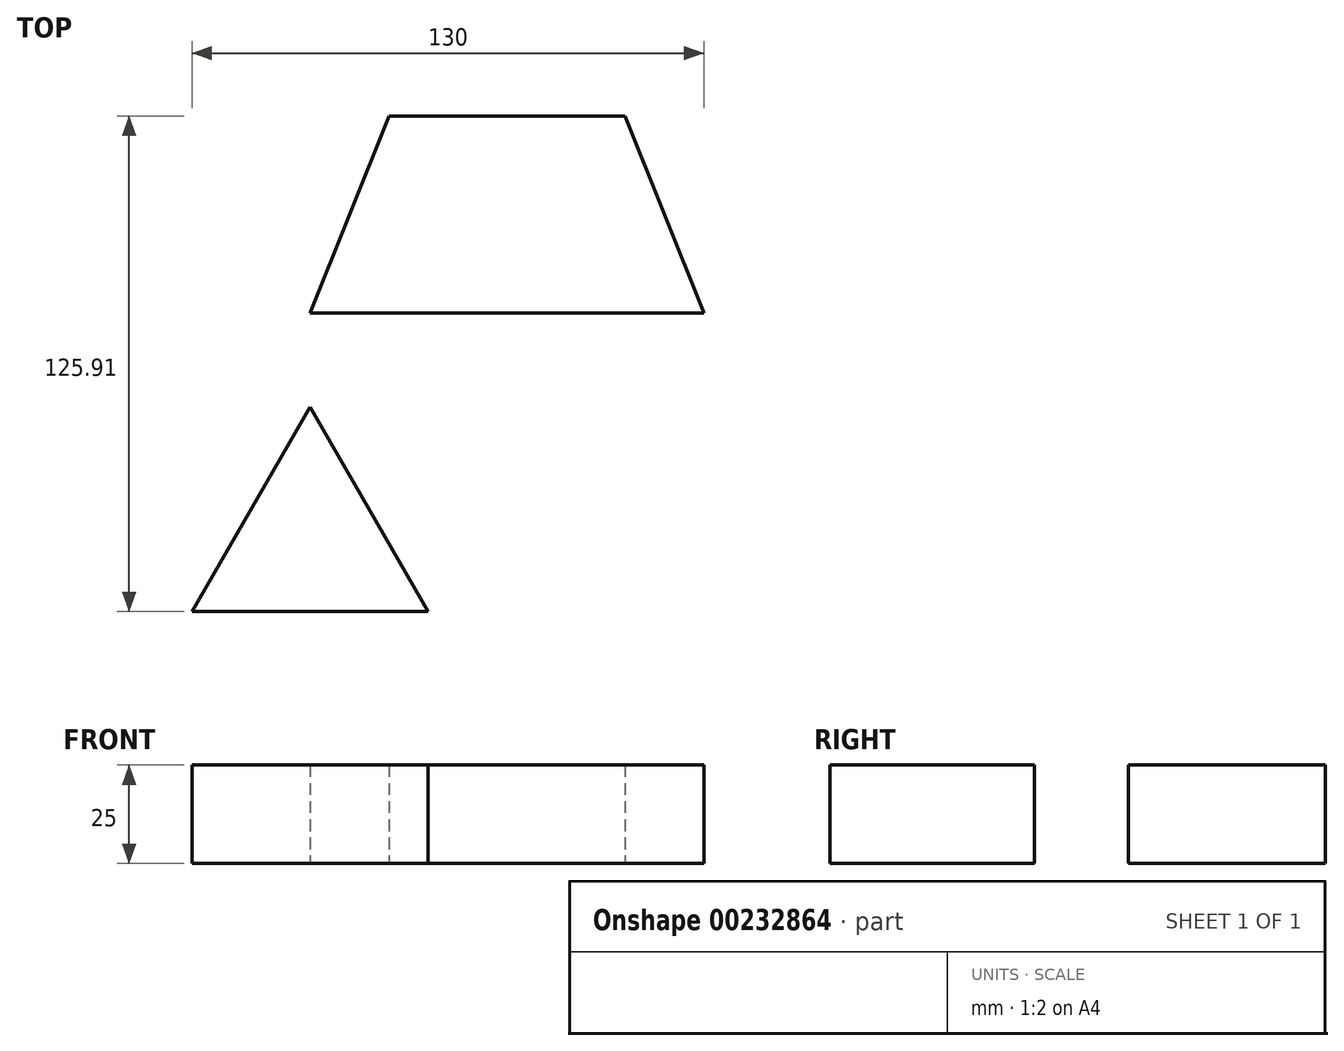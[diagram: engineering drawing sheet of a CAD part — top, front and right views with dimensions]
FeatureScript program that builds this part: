
annotation { "Feature Type Name" : "Feature", "Feature Type Description" : "" }
export const myFeature = defineFeature(function(context is Context, id is Id, definition is map)
    precondition{}
    {
        {
            var Q0;
            Q0=qCreatedBy(makeId("Top.planeOp"),FACE);
            var sketch = newSketch(context, id + "F0", { "sketchPlane" : qUnion([Q0])});
            skLineSegment(sketch, "E0", {"start": v(0, 0) * mm, "end": v(-30, -51.96) * mm});
            skLineSegment(sketch, "E1", {"start": v(-30, -51.96) * mm, "end": v(30, -51.96) * mm});
            skLineSegment(sketch, "E2", {"start": v(30, -51.96) * mm, "end": v(0, 0) * mm});
            skLineSegment(sketch, "E3", {"start": v(0, 23.95) * mm, "end": v(100, 23.95) * mm});
            skLineSegment(sketch, "E4", {"start": v(100, 23.95) * mm, "end": v(80, 73.95) * mm});
            skLineSegment(sketch, "E5", {"start": v(80, 73.95) * mm, "end": v(20, 73.95) * mm});
            skLineSegment(sketch, "E6", {"start": v(20, 73.95) * mm, "end": v(0, 23.95) * mm});
            skLineSegment(sketch, "E7", {"start": v(-134.7, 14.67) * mm, "end": v(-54.7, 14.67) * mm});
            skLineSegment(sketch, "E8", {"start": v(-54.7, 14.67) * mm, "end": v(-24.7, 66.63) * mm});
            skLineSegment(sketch, "E9", {"start": v(-134.7, 14.67) * mm, "end": v(-110.76, 80.45) * mm});
            skLineSegment(sketch, "E10", {"start": v(-110.76, 80.45) * mm, "end": v(-85.6, 68.18) * mm});
            skLineSegment(sketch, "E11", {"start": v(-110.76, 80.45) * mm, "end": v(-65.12, 80.45) * mm});
            skSolve(sketch);
        }
        {
            var Q0;
            Q0 = qSketchRegion(id + "F0", true);
            extrude(context, id + "F1", {"entities" : qUnion([Q0]), "depth" : 25 * mm});
        }
        {
            var Q0;
            Q0 = qSketchRegion(id + "F0", true);
            extrude(context, id + "F2", {"entities" : qUnion([Q0]), "depth" : 25 * mm});
        }
    });
